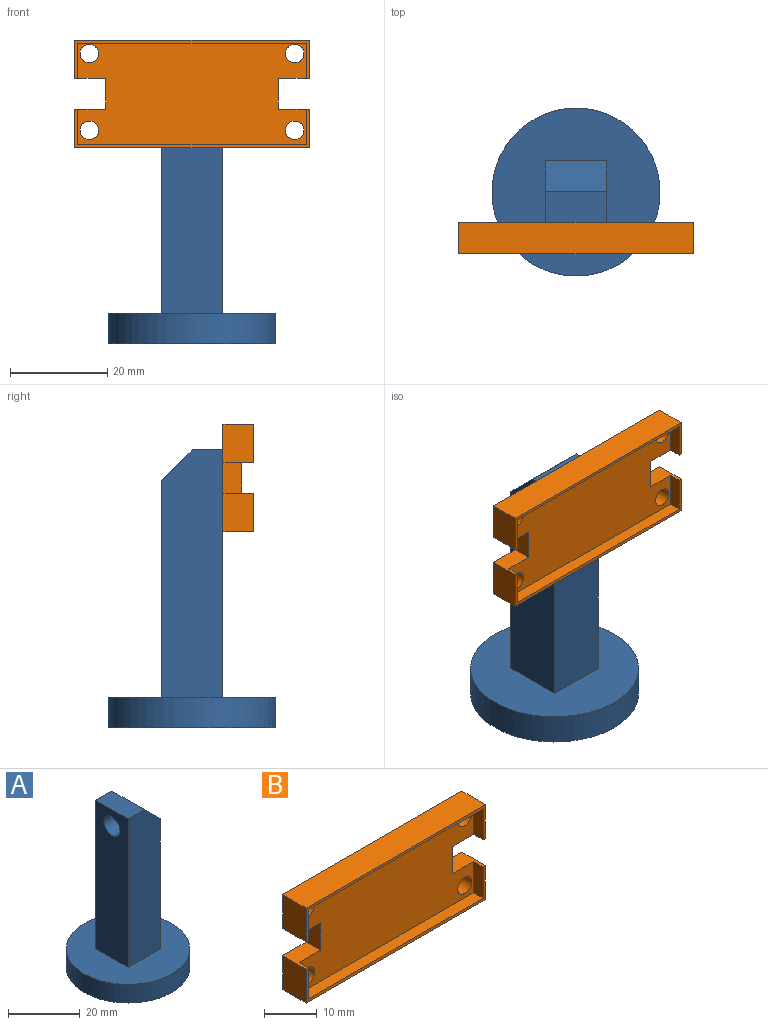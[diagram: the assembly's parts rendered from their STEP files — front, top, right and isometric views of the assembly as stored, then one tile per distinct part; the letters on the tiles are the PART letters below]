
ASSEMBLY  parts=2 mates=1
PART A: 11 faces, bbox 34.5x34.5x57.2 mm
  f0: plane 34.54x34.54mm, normal (0,0,1), area 775.9mm2, adj f1,f3,f4,f5,f6
  f1: cylinder r=17.27mm len=34.54mm, axis (0,0,-1), area 689.1mm2, adj f0,f2
  f2: plane 34.54x34.54mm, normal (0,0,-1), area 937.2mm2, adj f1
  f3: plane 44.45x12.7mm, normal (1,0,0), area 564.5mm2, adj f0,f4,f6,f8
  f4: plane 50.8x12.7mm, normal (0,1,0), area 625mm2, adj f0,f3,f5,f7,f8
  f5: plane 50.8x12.7mm, normal (-1,0,0), area 613.5mm2, adj f0,f4,f6,f7,f9
  f6: plane 50.8x12.7mm, normal (0,-1,0), area 625mm2, adj f0,f3,f5,f7,f8
  f7: plane 12.7x6.35mm, normal (0,0,1), area 80.6mm2, adj f4,f5,f6,f8
  f8: plane 12.7x6.35mm, normal (0.71,0,0.71), area 114mm2, adj f3,f4,f6,f7
  f9: cylinder r=3.17mm len=6.35mm, axis (-1,0,0), area 126.7mm2, adj f5,f10
  f10: plane 6.35x6.35mm, normal (-1,0,0), area 31.7mm2, adj f9
PART B: 28 faces, bbox 48.3x12.7x22.1 mm
  f0: plane 48.26x7.87mm, normal (0,-1,0), area 39.8mm2, adj f2,f6,f12,f15,f17,f18,f23,f27
  f1: plane 48.26x7.87mm, normal (0,-1,0), area 39.8mm2, adj f3,f5,f13,f14,f16,f19,f22,f26
  f2: plane 7.87x6.35mm, normal (1,0,0), area 50mm2, adj f0,f4,f12,f27
  f3: plane 7.87x6.35mm, normal (-1,0,0), area 50mm2, adj f1,f4,f14,f22
  f4: plane 48.26x22.1mm, normal (0,1,0), area 908.5mm2, adj f2,f3,f8,f9,f10,f11,f12,f13
  f5: plane 7.24x2.54mm, normal (1,0,0), area 18.4mm2, adj f1,f7,f16,f22
  f6: plane 7.24x2.54mm, normal (-1,0,0), area 18.4mm2, adj f0,f7,f18,f27
  f7: plane 46.99x20.83mm, normal (0,-1,0), area 860.5mm2, adj f5,f6,f8,f9,f10,f11,f16,f17
  f8: cylinder r=1.91mm len=3.81mm, axis (0,1,0), area 45.6mm2, adj f4,f7
  f9: cylinder r=1.91mm len=3.81mm, axis (0,1,0), area 45.6mm2, adj f4,f7
  f10: cylinder r=1.91mm len=3.81mm, axis (0,1,0), area 45.6mm2, adj f4,f7
  f11: cylinder r=1.91mm len=3.81mm, axis (0,1,0), area 45.6mm2, adj f4,f7
  f12: plane 48.26x6.35mm, normal (0,0,-1), area 306.5mm2, adj f0,f2,f4,f15
  f13: plane 7.87x6.35mm, normal (1,0,0), area 50mm2, adj f1,f4,f14,f26
  f14: plane 48.26x6.35mm, normal (0,0,1), area 306.5mm2, adj f1,f3,f4,f13
  f15: plane 7.87x6.35mm, normal (-1,0,0), area 50mm2, adj f0,f4,f12,f23
  f16: plane 46.99x2.54mm, normal (0,0,-1), area 119.4mm2, adj f1,f5,f7,f19
  f17: plane 7.24x2.54mm, normal (1,0,0), area 18.4mm2, adj f0,f7,f18,f23
  f18: plane 46.99x2.54mm, normal (0,0,1), area 119.4mm2, adj f0,f6,f7,f17
  f19: plane 7.24x2.54mm, normal (-1,0,0), area 18.4mm2, adj f1,f7,f16,f26
  f20: cylinder r=3.17mm len=6.35mm, axis (0,-1,0), area 126.7mm2, adj f4,f21
  f21: plane 6.35x6.35mm, normal (0,1,0), area 31.7mm2, adj f20
  f22: plane 6.35x6.35mm, normal (0,0,-1), area 25.8mm2, adj f1,f3,f4,f5,f7,f24
  f23: plane 6.35x6.35mm, normal (0,0,1), area 25.8mm2, adj f0,f4,f7,f15,f17,f24
  f24: plane 6.35x3.81mm, normal (-1,0,0), area 24.2mm2, adj f4,f7,f22,f23
  f25: plane 6.35x3.81mm, normal (1,0,0), area 24.2mm2, adj f4,f7,f26,f27
  f26: plane 6.35x6.35mm, normal (0,0,-1), area 25.8mm2, adj f1,f4,f7,f13,f19,f25
  f27: plane 6.35x6.35mm, normal (0,0,1), area 25.8mm2, adj f0,f2,f4,f6,f7,f25
PLACE A rot(axis=(0,0,1),90deg) t=(7.46,18.44,-22.23)mm
PLACE B rot(axis=(0,0,1),0deg) t=(7.46,12.09,29.2)mm
MATE fastened B.f20 <-> A.f9  axis (0,1,0) through (7.46,18.44,29.2)mm
